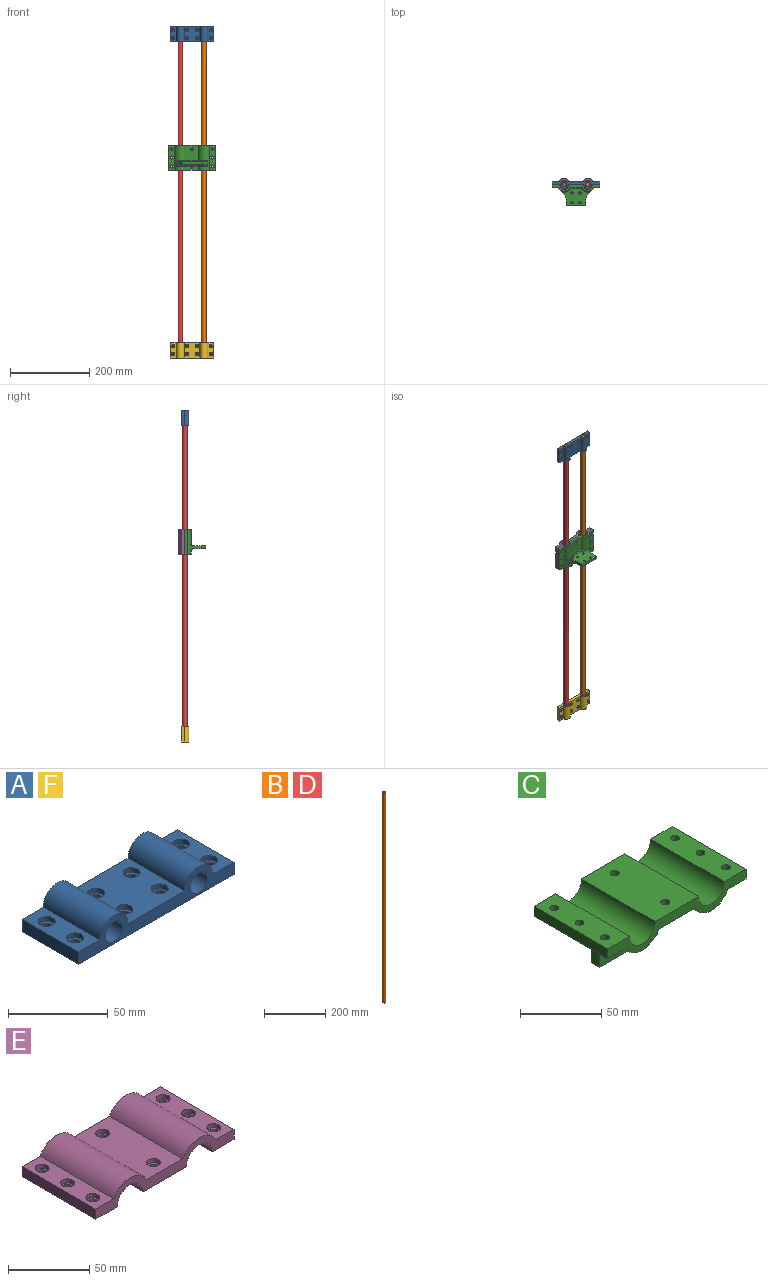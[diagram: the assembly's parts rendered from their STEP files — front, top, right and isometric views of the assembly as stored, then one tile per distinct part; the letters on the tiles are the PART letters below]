
ASSEMBLY  parts=6 mates=5
PART A: 36 faces, bbox 110x40x17.5 mm
  f0: plane 110x40mm, normal (0,0,-1), area 4209.9mm2, adj f2,f3,f10,f11,f28,f29,f30,f31
  f1: plane 40x40mm, normal (0,0,1), area 1373mm2, adj f5,f6,f10,f11,f16,f18,f20,f22
  f2: plane 40x7.5mm, normal (-1,0,0), area 300mm2, adj f0,f9,f10,f11
  f3: plane 40x7.5mm, normal (1,0,0), area 300mm2, adj f0,f4,f10,f11
  f4: plane 40x15mm, normal (0,0,1), area 486.5mm2, adj f3,f5,f10,f11,f24,f26
  f5: cylinder r=10mm len=40mm, axis (0,1,0), area 1256.6mm2, adj f1,f4,f10,f11
  f6: cylinder r=10mm len=40mm, axis (0,1,0), area 1256.6mm2, adj f1,f9,f10,f11
  f7: cylinder r=6.05mm len=40mm, axis (0,1,0), area 1520.5mm2, adj f10,f11
  f8: cylinder r=6.05mm len=40mm, axis (0,1,0), area 1520.5mm2, adj f10,f11
  f9: plane 40x15mm, normal (0,0,1), area 486.5mm2, adj f2,f6,f10,f11,f12,f14
  f10: plane 110x17.5mm, normal (0,-1,0), area 909.2mm2, adj f0,f1,f2,f3,f4,f5,f6,f7
  f11: plane 110x17.5mm, normal (0,1,0), area 909.2mm2, adj f0,f1,f2,f3,f4,f5,f6,f7
  f12: cylinder r=4.25mm len=8.5mm, axis (0,0,1), area 80.1mm2, adj f9,f13
  f13: plane 8.5x8.5mm, normal (0,0,1), area 33mm2, adj f12,f35
  f14: cylinder r=4.25mm len=8.5mm, axis (0,0,1), area 80.1mm2, adj f9,f15
  f15: plane 8.5x8.5mm, normal (0,0,1), area 33mm2, adj f14,f34
  f16: cylinder r=4.25mm len=8.5mm, axis (0,0,1), area 80.1mm2, adj f1,f17
  f17: plane 8.5x8.5mm, normal (0,0,1), area 33mm2, adj f16,f33
  f18: cylinder r=4.25mm len=8.5mm, axis (0,0,1), area 80.1mm2, adj f1,f19
  f19: plane 8.5x8.5mm, normal (0,0,1), area 33mm2, adj f18,f32
  f20: cylinder r=4.25mm len=8.5mm, axis (0,0,1), area 80.1mm2, adj f1,f21
  f21: plane 8.5x8.5mm, normal (0,0,1), area 33mm2, adj f20,f31
  f22: cylinder r=4.25mm len=8.5mm, axis (0,0,1), area 80.1mm2, adj f1,f23
  f23: plane 8.5x8.5mm, normal (0,0,1), area 33mm2, adj f22,f30
  f24: cylinder r=4.25mm len=8.5mm, axis (0,0,1), area 80.1mm2, adj f4,f25
  f25: plane 8.5x8.5mm, normal (0,0,1), area 33mm2, adj f24,f29
  f26: cylinder r=4.25mm len=8.5mm, axis (0,0,1), area 80.1mm2, adj f4,f27
  f27: plane 8.5x8.5mm, normal (0,0,1), area 33mm2, adj f26,f28
  f28: cylinder r=2.75mm len=5.5mm, axis (0,0,1), area 77.8mm2, adj f0,f27
  f29: cylinder r=2.75mm len=5.5mm, axis (0,0,1), area 77.8mm2, adj f0,f25
  f30: cylinder r=2.75mm len=5.5mm, axis (0,0,1), area 77.8mm2, adj f0,f23
  f31: cylinder r=2.75mm len=5.5mm, axis (0,0,1), area 77.8mm2, adj f0,f21
  f32: cylinder r=2.75mm len=5.5mm, axis (0,0,1), area 77.8mm2, adj f0,f19
  f33: cylinder r=2.75mm len=5.5mm, axis (0,0,1), area 77.8mm2, adj f0,f17
  f34: cylinder r=2.75mm len=5.5mm, axis (0,0,1), area 77.8mm2, adj f0,f15
  f35: cylinder r=2.75mm len=5.5mm, axis (0,0,1), area 77.8mm2, adj f0,f13
PART B: 5 faces, bbox 12x12x840 mm
  f0: cylinder r=6mm len=838mm, axis (0,0,-1), area 31591.9mm2, adj f3,f4
  f1: plane 10x10mm, normal (0,0,1), area 78.5mm2, adj f4
  f2: plane 10x10mm, normal (0,0,-1), area 78.5mm2, adj f3
  f3: cone r=6mm half-angle=45deg, axis (0,0,1), area 48.9mm2, adj f0,f2
  f4: cone r=5mm half-angle=45deg, axis (0,0,-1), area 48.9mm2, adj f0,f1
PART C: 96 faces, bbox 120x64x52.5 mm
  f0: plane 64x15.73mm, normal (0,0,-1), area 840.1mm2, adj f11,f12,f21,f22,f32,f33,f34,f35
  f1: cylinder r=2.75mm len=5.5mm, axis (0,0,-1), area 77.8mm2, adj f17,f81
  f2: cylinder r=2.75mm len=5.5mm, axis (0,0,-1), area 77.8mm2, adj f17,f74
  f3: cylinder r=2.75mm len=5.5mm, axis (0,0,-1), area 77.8mm2, adj f17,f67
  f4: cylinder r=2.75mm len=5.5mm, axis (0,0,-1), area 77.8mm2, adj f15,f60
  f5: cylinder r=2.75mm len=5.5mm, axis (0,0,-1), area 77.8mm2, adj f15,f53
  f6: cylinder r=2.75mm len=5.5mm, axis (0,0,-1), area 77.8mm2, adj f13,f52
  f7: cylinder r=2.75mm len=5.5mm, axis (0,0,-1), area 77.8mm2, adj f13,f45
  f8: cylinder r=2.75mm len=5.5mm, axis (0,0,-1), area 77.8mm2, adj f13,f38
  f9: plane 31.45x9.5mm, normal (0,0,-1), area 275.5mm2, adj f11,f20,f22,f54,f55,f56,f94
  f10: plane 39.5x31.45mm, normal (0,0,-1), area 1186.9mm2, adj f11,f20,f21,f61,f62,f63,f64,f65
  f11: cylinder r=16.12mm len=64mm, axis (0,1,0), area 1829mm2, adj f0,f9,f10,f21,f22,f89,f92,f95
  f12: plane 64x7.5mm, normal (1,0,0), area 480mm2, adj f0,f13,f21,f22
  f13: plane 64x18.88mm, normal (0,0,1), area 1136.7mm2, adj f6,f7,f8,f12,f14,f21,f22
  f14: cylinder r=11.12mm len=64mm, axis (0,1,0), area 2236.8mm2, adj f13,f15,f21,f22
  f15: plane 64x37.75mm, normal (0,0,1), area 2368.5mm2, adj f4,f5,f14,f16,f21,f22
  f16: cylinder r=11.12mm len=64mm, axis (0,1,0), area 2236.8mm2, adj f15,f17,f21,f22
  f17: plane 64x18.88mm, normal (0,0,1), area 1136.7mm2, adj f1,f2,f3,f16,f18,f21,f22
  f18: plane 64x7.5mm, normal (-1,0,0), area 480mm2, adj f17,f19,f21,f22
  f19: plane 64x15.73mm, normal (0,0,-1), area 840.1mm2, adj f18,f20,f21,f22,f68,f69,f70,f71
  f20: cylinder r=16.12mm len=64mm, axis (0,1,0), area 1829mm2, adj f9,f10,f19,f21,f22,f88,f90,f93
  f21: plane 120x16.13mm, normal (0,-1,0), area 862.3mm2, adj f0,f10,f11,f12,f13,f14,f15,f16
  f22: plane 120x16.13mm, normal (0,1,0), area 862.3mm2, adj f0,f9,f11,f12,f13,f14,f15,f16
  f23: plane 67.51x42.5mm, normal (0,-1,0), area 2046.9mm2, adj f24,f25,f26,f28,f29,f30,f31,f88
  f24: plane 50x7.5mm, normal (0,0,-1), area 375mm2, adj f23,f25,f26,f27
  f25: plane 11.1x7.5mm, normal (1,0,0), area 83.3mm2, adj f23,f24,f27,f89
  f26: plane 11.1x7.5mm, normal (-1,0,0), area 83.3mm2, adj f23,f24,f27,f88
  f27: plane 63.01x40mm, normal (0,1,0), area 1869.6mm2, adj f24,f25,f26,f28,f29,f30,f31,f88
  f28: cylinder r=2.75mm len=7.5mm, axis (0,-1,0), area 129.6mm2, adj f23,f27
  f29: cylinder r=2.75mm len=7.5mm, axis (0,-1,0), area 129.6mm2, adj f23,f27
  f30: cylinder r=2.75mm len=7.5mm, axis (0,-1,0), area 129.6mm2, adj f23,f27
  f31: cylinder r=2.75mm len=7.5mm, axis (0,-1,0), area 129.6mm2, adj f23,f27
  f32: plane 4x3mm, normal (0.5,0.87,0), area 13.9mm2, adj f0,f33,f37,f38
  f33: plane 4.62x3mm, normal (1,0,0), area 13.9mm2, adj f0,f32,f34,f38
  f34: plane 4x3mm, normal (0.5,-0.87,0), area 13.9mm2, adj f0,f33,f35,f38
  f35: plane 4x3mm, normal (-0.5,-0.87,0), area 13.9mm2, adj f0,f34,f36,f38
  f36: plane 4.62x3mm, normal (-1,0,0), area 13.9mm2, adj f0,f35,f37,f38
  f37: plane 4x3mm, normal (-0.5,0.87,0), area 13.9mm2, adj f0,f32,f36,f38
  f38: plane 9.24x8mm, normal (0,0,-1), area 31.7mm2, adj f8,f32,f33,f34,f35,f36,f37
  f39: plane 4x3mm, normal (0.5,-0.87,0), area 13.9mm2, adj f0,f40,f44,f45
  f40: plane 4x3mm, normal (-0.5,-0.87,0), area 13.9mm2, adj f0,f39,f41,f45
  f41: plane 4.62x3mm, normal (-1,0,0), area 13.9mm2, adj f0,f40,f42,f45
  f42: plane 4x3mm, normal (-0.5,0.87,0), area 13.9mm2, adj f0,f41,f43,f45
  f43: plane 4x3mm, normal (0.5,0.87,0), area 13.9mm2, adj f0,f42,f44,f45
  f44: plane 4.62x3mm, normal (1,0,0), area 13.9mm2, adj f0,f39,f43,f45
  f45: plane 9.24x8mm, normal (0,0,-1), area 31.7mm2, adj f7,f39,f40,f41,f42,f43,f44
  f46: plane 4x3mm, normal (0.5,-0.87,0), area 13.9mm2, adj f0,f47,f51,f52
  f47: plane 4x3mm, normal (-0.5,-0.87,0), area 13.9mm2, adj f0,f46,f48,f52
  f48: plane 4.62x3mm, normal (-1,0,0), area 13.9mm2, adj f0,f47,f49,f52
  f49: plane 4x3mm, normal (-0.5,0.87,0), area 13.9mm2, adj f0,f48,f50,f52
  f50: plane 4x3mm, normal (0.5,0.87,0), area 13.9mm2, adj f0,f49,f51,f52
  f51: plane 4.62x3mm, normal (1,0,0), area 13.9mm2, adj f0,f46,f50,f52
  f52: plane 9.24x8mm, normal (0,0,-1), area 31.7mm2, adj f6,f46,f47,f48,f49,f50,f51
  f53: plane 9.24x8mm, normal (0,0,-1), area 31.7mm2, adj f5,f54,f55,f56,f57,f58,f59
  f54: plane 4x3.03mm, normal (0.87,-0.5,0), area 13.9mm2, adj f9,f53,f55,f59,f94
  f55: plane 4.62x3mm, normal (0,-1,0), area 13.9mm2, adj f9,f53,f54,f56
  f56: plane 4x3.03mm, normal (-0.87,-0.5,0), area 13.9mm2, adj f9,f53,f55,f57,f94
  f57: plane 5.82x4mm, normal (-0.87,0.5,0), area 18mm2, adj f53,f56,f58,f94
  f58: plane 5.82x4.62mm, normal (0,1,0), area 26.9mm2, adj f53,f57,f59,f94
  f59: plane 5.82x4mm, normal (0.87,0.5,0), area 18mm2, adj f53,f54,f58,f94
  f60: plane 9.24x8mm, normal (0,0,-1), area 31.7mm2, adj f4,f61,f62,f63,f64,f65,f66
  f61: plane 4x3mm, normal (-0.5,-0.87,0), area 13.9mm2, adj f10,f60,f62,f66
  f62: plane 4.62x3mm, normal (-1,0,0), area 13.9mm2, adj f10,f60,f61,f63
  f63: plane 4x3mm, normal (-0.5,0.87,0), area 13.9mm2, adj f10,f60,f62,f64
  f64: plane 4x3mm, normal (0.5,0.87,0), area 13.9mm2, adj f10,f60,f63,f65
  f65: plane 4.62x3mm, normal (1,0,0), area 13.9mm2, adj f10,f60,f64,f66
  f66: plane 4x3mm, normal (0.5,-0.87,0), area 13.9mm2, adj f10,f60,f61,f65
  f67: plane 9.24x8mm, normal (0,0,-1), area 31.7mm2, adj f3,f68,f69,f70,f71,f72,f73
  f68: plane 4x3mm, normal (-0.5,-0.87,0), area 13.9mm2, adj f19,f67,f69,f73
  f69: plane 4.62x3mm, normal (-1,0,0), area 13.9mm2, adj f19,f67,f68,f70
  f70: plane 4x3mm, normal (-0.5,0.87,0), area 13.9mm2, adj f19,f67,f69,f71
  f71: plane 4x3mm, normal (0.5,0.87,0), area 13.9mm2, adj f19,f67,f70,f72
  f72: plane 4.62x3mm, normal (1,0,0), area 13.9mm2, adj f19,f67,f71,f73
  f73: plane 4x3mm, normal (0.5,-0.87,0), area 13.9mm2, adj f19,f67,f68,f72
  f74: plane 9.24x8mm, normal (0,0,-1), area 31.7mm2, adj f2,f75,f76,f77,f78,f79,f80
  f75: plane 4x3mm, normal (-0.5,-0.87,0), area 13.9mm2, adj f19,f74,f76,f80
  f76: plane 4.62x3mm, normal (-1,0,0), area 13.9mm2, adj f19,f74,f75,f77
  f77: plane 4x3mm, normal (-0.5,0.87,0), area 13.9mm2, adj f19,f74,f76,f78
  f78: plane 4x3mm, normal (0.5,0.87,0), area 13.9mm2, adj f19,f74,f77,f79
  f79: plane 4.62x3mm, normal (1,0,0), area 13.9mm2, adj f19,f74,f78,f80
  f80: plane 4x3mm, normal (0.5,-0.87,0), area 13.9mm2, adj f19,f74,f75,f79
  f81: plane 9.24x8mm, normal (0,0,-1), area 31.7mm2, adj f1,f82,f83,f84,f85,f86,f87
  f82: plane 4x3mm, normal (-0.5,-0.87,0), area 13.9mm2, adj f19,f81,f83,f87
  f83: plane 4.62x3mm, normal (-1,0,0), area 13.9mm2, adj f19,f81,f82,f84
  f84: plane 4x3mm, normal (-0.5,0.87,0), area 13.9mm2, adj f19,f81,f83,f85
  f85: plane 4x3mm, normal (0.5,0.87,0), area 13.9mm2, adj f19,f81,f84,f86
  f86: plane 4.62x3mm, normal (1,0,0), area 13.9mm2, adj f19,f81,f85,f87
  f87: plane 4x3mm, normal (0.5,-0.87,0), area 13.9mm2, adj f19,f81,f82,f86
  f88: cylinder r=35mm len=28.34mm, axis (0,1,0), area 276.2mm2, adj f20,f23,f26,f27,f90,f93
  f89: cylinder r=35mm len=28.34mm, axis (0,1,0), area 276.2mm2, adj f11,f23,f25,f27,f92,f95
  f90: torus R=18.62mm, axis (0,1,0), area 96.6mm2, adj f20,f23,f88,f91
  f91: cylinder r=2.5mm len=31.45mm, axis (-1,0,0), area 119.3mm2, adj f10,f23,f90,f92
  f92: torus R=18.62mm, axis (0,1,0), area 96.6mm2, adj f11,f23,f89,f91
  f93: torus R=21.12mm, axis (0,-1,0), area 186.3mm2, adj f20,f27,f88,f94
  f94: cylinder r=5mm len=31.45mm, axis (1,0,0), area 192.4mm2, adj f9,f27,f54,f56,f57,f58,f59,f93
  f95: torus R=21.12mm, axis (0,-1,0), area 186.3mm2, adj f11,f27,f89,f94
PART D: same geometry as B
PART E: 38 faces, bbox 120x64x16.1 mm
  f0: cylinder r=11.12mm len=64mm, axis (0,1,0), area 2236.8mm2, adj f1,f11,f12,f13
  f1: plane 64x37.75mm, normal (0,0,-1), area 2368.5mm2, adj f0,f2,f12,f13,f33,f34
  f2: cylinder r=11.12mm len=64mm, axis (0,1,0), area 2236.8mm2, adj f1,f3,f12,f13
  f3: plane 64x18.88mm, normal (0,0,-1), area 1136.7mm2, adj f2,f4,f12,f13,f30,f31,f32
  f4: plane 64x7.5mm, normal (1,0,0), area 480mm2, adj f3,f5,f12,f13
  f5: plane 64x15.73mm, normal (0,0,1), area 836.2mm2, adj f4,f6,f12,f13,f24,f26,f28
  f6: cylinder r=16.12mm len=64mm, axis (0,1,0), area 2243.6mm2, adj f5,f7,f12,f13
  f7: plane 64x31.45mm, normal (0,0,1), area 1899.4mm2, adj f6,f8,f12,f13,f20,f22
  f8: cylinder r=16.12mm len=64mm, axis (0,1,0), area 2243.6mm2, adj f7,f9,f12,f13
  f9: plane 64x15.73mm, normal (0,0,1), area 836.2mm2, adj f8,f10,f12,f13,f14,f16,f18
  f10: plane 64x7.5mm, normal (-1,0,0), area 480mm2, adj f9,f11,f12,f13
  f11: plane 64x18.88mm, normal (0,0,-1), area 1136.7mm2, adj f0,f10,f12,f13,f35,f36,f37
  f12: plane 120x16.13mm, normal (0,-1,0), area 862.3mm2, adj f0,f1,f2,f3,f4,f5,f6,f7
  f13: plane 120x16.13mm, normal (0,1,0), area 862.3mm2, adj f0,f1,f2,f3,f4,f5,f6,f7
  f14: cylinder r=4.25mm len=8.5mm, axis (0,0,1), area 80.1mm2, adj f9,f15
  f15: plane 8.5x8.5mm, normal (0,0,1), area 33mm2, adj f14,f37
  f16: cylinder r=4.25mm len=8.5mm, axis (0,0,1), area 80.1mm2, adj f9,f17
  f17: plane 8.5x8.5mm, normal (0,0,1), area 33mm2, adj f16,f36
  f18: cylinder r=4.25mm len=8.5mm, axis (0,0,1), area 80.1mm2, adj f9,f19
  f19: plane 8.5x8.5mm, normal (0,0,1), area 33mm2, adj f18,f35
  f20: cylinder r=4.25mm len=8.5mm, axis (0,0,1), area 80.1mm2, adj f7,f21
  f21: plane 8.5x8.5mm, normal (0,0,1), area 33mm2, adj f20,f34
  f22: cylinder r=4.25mm len=8.5mm, axis (0,0,1), area 80.1mm2, adj f7,f23
  f23: plane 8.5x8.5mm, normal (0,0,1), area 33mm2, adj f22,f33
  f24: cylinder r=4.25mm len=8.5mm, axis (0,0,1), area 80.1mm2, adj f5,f25
  f25: plane 8.5x8.5mm, normal (0,0,1), area 33mm2, adj f24,f32
  f26: cylinder r=4.25mm len=8.5mm, axis (0,0,1), area 80.1mm2, adj f5,f27
  f27: plane 8.5x8.5mm, normal (0,0,1), area 33mm2, adj f26,f31
  f28: cylinder r=4.25mm len=8.5mm, axis (0,0,1), area 80.1mm2, adj f5,f29
  f29: plane 8.5x8.5mm, normal (0,0,1), area 33mm2, adj f28,f30
  f30: cylinder r=2.75mm len=5.5mm, axis (0,0,1), area 77.8mm2, adj f3,f29
  f31: cylinder r=2.75mm len=5.5mm, axis (0,0,1), area 77.8mm2, adj f3,f27
  f32: cylinder r=2.75mm len=5.5mm, axis (0,0,1), area 77.8mm2, adj f3,f25
  f33: cylinder r=2.75mm len=5.5mm, axis (0,0,1), area 77.8mm2, adj f1,f23
  f34: cylinder r=2.75mm len=5.5mm, axis (0,0,1), area 77.8mm2, adj f1,f21
  f35: cylinder r=2.75mm len=5.5mm, axis (0,0,1), area 77.8mm2, adj f11,f19
  f36: cylinder r=2.75mm len=5.5mm, axis (0,0,1), area 77.8mm2, adj f11,f17
  f37: cylinder r=2.75mm len=5.5mm, axis (0,0,1), area 77.8mm2, adj f11,f15
PART F: same geometry as A
PLACE A rot(axis=(1,0,0),90deg) t=(0,-7.5,800)mm
PLACE B t=(30,-7.5,400)mm
PLACE C rot(axis=(-1,0,0),90deg) t=(0,-7.5,486.57)mm
PLACE D t=(-30,-7.5,400)mm
PLACE E rot(axis=(-1,0,0),90deg) t=(0,-7.5,486.57)mm
PLACE F rot(axis=(1,0,0),90deg) t=(0,-7.5,0)mm
MATE slider F.f5 <-> E.f2  axis (0,0,-1) through (30,-7.5,-20)mm
MATE fastened E.f11 <-> C.f17  axis (0,-1,0) through (-60,-7.5,518.57)mm
MATE fastened F.f8 <-> B.f0  axis (0,0,-1) through (30,-7.5,-20)mm
MATE fastened A.f8 <-> B.f0  axis (0,0,1) through (30,-7.5,820)mm
MATE fastened F.f7 <-> D.f0  axis (0,0,-1) through (-30,-7.5,-20)mm
